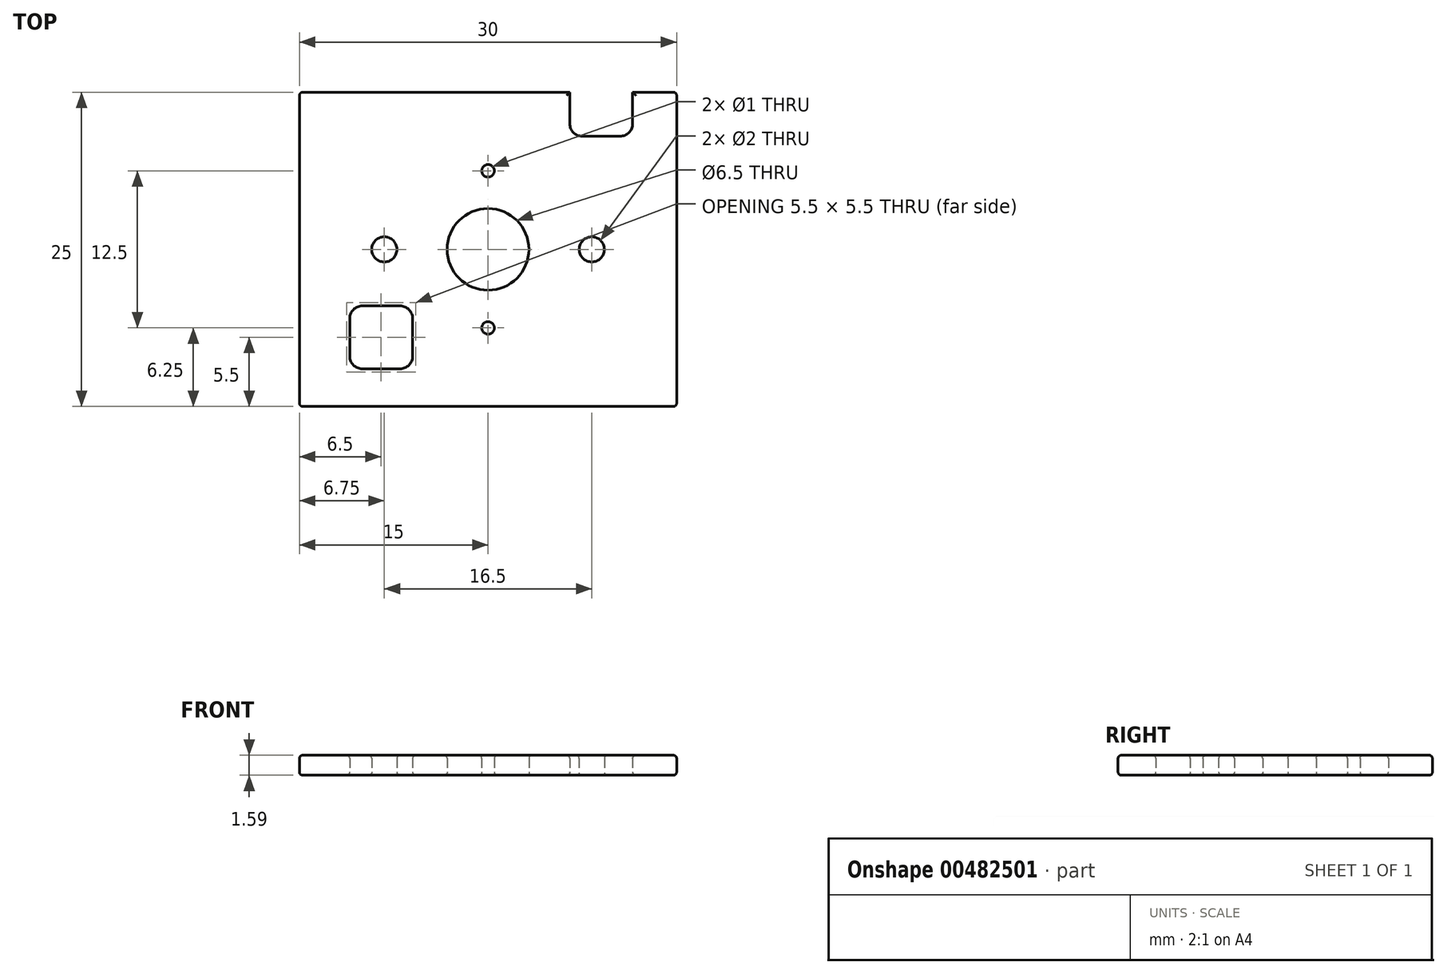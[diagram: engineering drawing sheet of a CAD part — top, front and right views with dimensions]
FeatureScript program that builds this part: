
annotation { "Feature Type Name" : "Feature", "Feature Type Description" : "" }
export const myFeature = defineFeature(function(context is Context, id is Id, definition is map)
    precondition{}
    {
        {
            var Q0;
            Q0=qCreatedBy(makeId("Top.planeOp"),FACE);
            var sketch = newSketch(context, id + "F0", { "sketchPlane" : qUnion([Q0])});
            skLineSegment(sketch, "E0", {"start": v(0, 0) * mm, "end": v(30, 0) * mm});
            skLineSegment(sketch, "E1", {"start": v(30, 0) * mm, "end": v(30, 25) * mm});
            skLineSegment(sketch, "E2", {"start": v(30, 25) * mm, "end": v(26.5, 25) * mm});
            skLineSegment(sketch, "E3", {"start": v(26.5, 25) * mm, "end": v(26.5, 21.5) * mm});
            skLineSegment(sketch, "E4", {"start": v(26.5, 21.5) * mm, "end": v(21.5, 21.5) * mm});
            skLineSegment(sketch, "E5", {"start": v(21.5, 21.5) * mm, "end": v(21.5, 25) * mm});
            skLineSegment(sketch, "E6", {"start": v(21.5, 25) * mm, "end": v(0, 25) * mm});
            skLineSegment(sketch, "E7", {"start": v(0, 25) * mm, "end": v(0, 0) * mm});
            skLineSegment(sketch, "E8.bottom", {"start": v(4, 8) * mm, "end": v(9, 8) * mm});
            skLineSegment(sketch, "E8.top", {"start": v(4, 3) * mm, "end": v(9, 3) * mm});
            skLineSegment(sketch, "E8.left", {"start": v(4, 8) * mm, "end": v(4, 3) * mm});
            skLineSegment(sketch, "E8.right", {"start": v(9, 8) * mm, "end": v(9, 3) * mm});
            skLineSegment(sketch, "E9", {"start": v(-15, 12.5) * mm, "end": v(45, 12.5) * mm, "construction": true});
            skLineSegment(sketch, "E10", {"start": v(15, 37.5) * mm, "end": v(15, -12.5) * mm, "construction": true});
            skCircle(sketch, "E11", {"center": v(15, 12.5) * mm, "radius": 3.25 * mm});
            skCircle(sketch, "E12", {"center": v(15, 6.25) * mm, "radius": 0.5 * mm});
            skCircle(sketch, "E13", {"center": v(6.75, 12.5) * mm, "radius": 1 * mm});
            skCircle(sketch, "E14.MirrorC", {"center": v(15, 18.75) * mm, "radius": 0.5 * mm});
            skCircle(sketch, "E15.MirrorC", {"center": v(23.25, 12.5) * mm, "radius": 1 * mm});
            skSolve(sketch);
        }
        {
            var Q0;
            Q0 = qSketchRegion(id + "F0", true);
            extrude(context, id + "F1", {"entities" : qUnion([Q0]), "depth" : 1.59 * mm});
        }
        {
            var Q0;
            Q0=makeQuery(id+"F1.opExtrude","SWEPT_EDGE",EDGE,{"disambiguationData":[OSD([sQuery(id+"F0.wireOp",EDGE,"E8.bottom"),sQuery(id+"F0.wireOp",EDGE,"E8.left")])]});
            var Q1;
            Q1=makeQuery(id+"F1.opExtrude","SWEPT_EDGE",EDGE,{"disambiguationData":[OSD([sQuery(id+"F0.wireOp",EDGE,"E8.bottom"),sQuery(id+"F0.wireOp",EDGE,"E8.right")])]});
            var Q2;
            Q2=makeQuery(id+"F1.opExtrude","SWEPT_EDGE",EDGE,{"disambiguationData":[OSD([sQuery(id+"F0.wireOp",EDGE,"E8.top"),sQuery(id+"F0.wireOp",EDGE,"E8.right")])]});
            var Q3;
            Q3=makeQuery(id+"F1.opExtrude","SWEPT_EDGE",EDGE,{"disambiguationData":[OSD([sQuery(id+"F0.wireOp",EDGE,"E8.top"),sQuery(id+"F0.wireOp",EDGE,"E8.left")])]});
            var Q4;
            Q4=makeQuery(id+"F1.opExtrude","SWEPT_EDGE",EDGE,{"disambiguationData":[OSD([sQuery(id+"F0.wireOp",EDGE,"E4"),sQuery(id+"F0.wireOp",EDGE,"E5")])]});
            var Q5;
            Q5=makeQuery(id+"F1.opExtrude","SWEPT_EDGE",EDGE,{"disambiguationData":[OSD([sQuery(id+"F0.wireOp",EDGE,"E3"),sQuery(id+"F0.wireOp",EDGE,"E4")])]});
            fillet(context, id + "F2", {"entities" : qUnion([Q0, Q1, Q2, Q3, Q4, Q5]), "radius" : 1 * mm, "tangentPropagation" : true, "allowEdgeOverflow" : false});
        }
        {
            var Q0;
            Q0=makeQuery(id+"F1.opExtrude","CAP_EDGE",EDGE,{"disambiguationData":[OSD([sQuery(id+"F0.wireOp",EDGE,"E13")])],"isStart":false});
            var Q1;
            Q1=makeQuery(id+"F1.opExtrude","CAP_EDGE",EDGE,{"disambiguationData":[OSD([sQuery(id+"F0.wireOp",EDGE,"E13")])],"isStart":true});
            var Q2;
            Q2=makeQuery(id+"F1.opExtrude","CAP_EDGE",EDGE,{"disambiguationData":[OSD([sQuery(id+"F0.wireOp",EDGE,"E14.MirrorC")])],"isStart":false});
            var Q3;
            Q3=makeQuery(id+"F1.opExtrude","CAP_EDGE",EDGE,{"disambiguationData":[OSD([sQuery(id+"F0.wireOp",EDGE,"E14.MirrorC")])],"isStart":true});
            var Q4;
            Q4=makeQuery(id+"F1.opExtrude","CAP_EDGE",EDGE,{"disambiguationData":[OSD([sQuery(id+"F0.wireOp",EDGE,"E15.MirrorC")])],"isStart":false});
            var Q5;
            Q5=makeQuery(id+"F1.opExtrude","CAP_EDGE",EDGE,{"disambiguationData":[OSD([sQuery(id+"F0.wireOp",EDGE,"E12")])],"isStart":false});
            var Q6;
            Q6=makeQuery(id+"F1.opExtrude","CAP_EDGE",EDGE,{"disambiguationData":[OSD([sQuery(id+"F0.wireOp",EDGE,"E12")])],"isStart":true});
            var Q7;
            Q7=makeQuery(id+"F1.opExtrude","CAP_EDGE",EDGE,{"disambiguationData":[OSD([sQuery(id+"F0.wireOp",EDGE,"E11")])],"isStart":false});
            var Q8;
            Q8=makeQuery(id+"F1.opExtrude","CAP_EDGE",EDGE,{"disambiguationData":[OSD([sQuery(id+"F0.wireOp",EDGE,"E11")])],"isStart":true});
            var Q9;
            Q9=makeQuery(id+"F1.opExtrude","CAP_EDGE",EDGE,{"disambiguationData":[OSD([sQuery(id+"F0.wireOp",EDGE,"E8.bottom")])],"isStart":false});
            var Q10;
            {var subQ0=sQuery(id+"F0.wireOp",EDGE,"E8.left");var subQ1=sQuery(id+"F0.wireOp",EDGE,"E8.bottom");Q10=makeQuery(id+"F2.opFillet","BLEND_EDGE",EDGE,{"blendedFrom":[makeQuery(id+"F1.opExtrude","SWEPT_EDGE",EDGE,{"disambiguationData":[OSD([subQ1,subQ0])]}),makeQuery(id+"F1.opExtrude","CAP_FACE",FACE,{"disambiguationData":[OSD([sQuery(id+"F0.wireOp",EDGE,"E0"),sQuery(id+"F0.wireOp",EDGE,"E1"),sQuery(id+"F0.wireOp",EDGE,"E2"),sQuery(id+"F0.wireOp",EDGE,"E3"),sQuery(id+"F0.wireOp",EDGE,"E4"),sQuery(id+"F0.wireOp",EDGE,"E5"),sQuery(id+"F0.wireOp",EDGE,"E6"),sQuery(id+"F0.wireOp",EDGE,"E7"),subQ1,sQuery(id+"F0.wireOp",EDGE,"E8.top"),subQ0,sQuery(id+"F0.wireOp",EDGE,"E8.right"),sQuery(id+"F0.wireOp",EDGE,"E11"),sQuery(id+"F0.wireOp",EDGE,"E12"),sQuery(id+"F0.wireOp",EDGE,"E13"),sQuery(id+"F0.wireOp",EDGE,"E14.MirrorC"),sQuery(id+"F0.wireOp",EDGE,"E15.MirrorC")])],"isStart":false})],"blendedInto":[makeQuery(id+"F1.opExtrude","CAP_FACE",FACE,{"disambiguationData":[OSD([sQuery(id+"F0.wireOp",EDGE,"E0"),sQuery(id+"F0.wireOp",EDGE,"E1"),sQuery(id+"F0.wireOp",EDGE,"E2"),sQuery(id+"F0.wireOp",EDGE,"E3"),sQuery(id+"F0.wireOp",EDGE,"E4"),sQuery(id+"F0.wireOp",EDGE,"E5"),sQuery(id+"F0.wireOp",EDGE,"E6"),sQuery(id+"F0.wireOp",EDGE,"E7"),subQ1,sQuery(id+"F0.wireOp",EDGE,"E8.top"),subQ0,sQuery(id+"F0.wireOp",EDGE,"E8.right"),sQuery(id+"F0.wireOp",EDGE,"E11"),sQuery(id+"F0.wireOp",EDGE,"E12"),sQuery(id+"F0.wireOp",EDGE,"E13"),sQuery(id+"F0.wireOp",EDGE,"E14.MirrorC"),sQuery(id+"F0.wireOp",EDGE,"E15.MirrorC")])],"isStart":false})]});}
            var Q11;
            Q11=makeQuery(id+"F1.opExtrude","CAP_EDGE",EDGE,{"disambiguationData":[OSD([sQuery(id+"F0.wireOp",EDGE,"E5")])],"isStart":false});
            var Q12;
            Q12=makeQuery(id+"F1.opExtrude","CAP_EDGE",EDGE,{"disambiguationData":[OSD([sQuery(id+"F0.wireOp",EDGE,"E2")])],"isStart":false});
            var Q13;
            Q13=makeQuery(id+"F1.opExtrude","CAP_EDGE",EDGE,{"disambiguationData":[OSD([sQuery(id+"F0.wireOp",EDGE,"E6")])],"isStart":false});
            var Q14;
            Q14=makeQuery(id+"F1.opExtrude","CAP_EDGE",EDGE,{"disambiguationData":[OSD([sQuery(id+"F0.wireOp",EDGE,"E7")])],"isStart":false});
            var Q15;
            Q15=makeQuery(id+"F1.opExtrude","SWEPT_EDGE",EDGE,{"disambiguationData":[OSD([sQuery(id+"F0.wireOp",EDGE,"E6"),sQuery(id+"F0.wireOp",EDGE,"E7")])]});
            var Q16;
            Q16=makeQuery(id+"F1.opExtrude","SWEPT_EDGE",EDGE,{"disambiguationData":[OSD([sQuery(id+"F0.wireOp",EDGE,"E1"),sQuery(id+"F0.wireOp",EDGE,"E2")])]});
            var Q17;
            Q17=makeQuery(id+"F1.opExtrude","SWEPT_EDGE",EDGE,{"disambiguationData":[OSD([sQuery(id+"F0.wireOp",EDGE,"E0"),sQuery(id+"F0.wireOp",EDGE,"E1")])]});
            var Q18;
            Q18=makeQuery(id+"F1.opExtrude","SWEPT_EDGE",EDGE,{"disambiguationData":[OSD([sQuery(id+"F0.wireOp",EDGE,"E0"),sQuery(id+"F0.wireOp",EDGE,"E7")])]});
            var Q19;
            Q19=makeQuery(id+"F1.opExtrude","CAP_EDGE",EDGE,{"disambiguationData":[OSD([sQuery(id+"F0.wireOp",EDGE,"E0")])],"isStart":false});
            var Q20;
            Q20=makeQuery(id+"F1.opExtrude","CAP_EDGE",EDGE,{"disambiguationData":[OSD([sQuery(id+"F0.wireOp",EDGE,"E1")])],"isStart":false});
            var Q21;
            Q21=makeQuery(id+"F1.opExtrude","CAP_EDGE",EDGE,{"disambiguationData":[OSD([sQuery(id+"F0.wireOp",EDGE,"E4")])],"isStart":true});
            var Q22;
            {var subQ0=sQuery(id+"F0.wireOp",EDGE,"E4");var subQ1=sQuery(id+"F0.wireOp",EDGE,"E3");Q22=makeQuery(id+"F2.opFillet","BLEND_EDGE",EDGE,{"blendedFrom":[makeQuery(id+"F1.opExtrude","SWEPT_EDGE",EDGE,{"disambiguationData":[OSD([subQ1,subQ0])]}),makeQuery(id+"F1.opExtrude","CAP_FACE",FACE,{"disambiguationData":[OSD([sQuery(id+"F0.wireOp",EDGE,"E0"),sQuery(id+"F0.wireOp",EDGE,"E1"),sQuery(id+"F0.wireOp",EDGE,"E2"),subQ1,subQ0,sQuery(id+"F0.wireOp",EDGE,"E5"),sQuery(id+"F0.wireOp",EDGE,"E6"),sQuery(id+"F0.wireOp",EDGE,"E7"),sQuery(id+"F0.wireOp",EDGE,"E8.bottom"),sQuery(id+"F0.wireOp",EDGE,"E8.top"),sQuery(id+"F0.wireOp",EDGE,"E8.left"),sQuery(id+"F0.wireOp",EDGE,"E8.right"),sQuery(id+"F0.wireOp",EDGE,"E11"),sQuery(id+"F0.wireOp",EDGE,"E12"),sQuery(id+"F0.wireOp",EDGE,"E13"),sQuery(id+"F0.wireOp",EDGE,"E14.MirrorC"),sQuery(id+"F0.wireOp",EDGE,"E15.MirrorC")])],"isStart":true})],"blendedInto":[makeQuery(id+"F1.opExtrude","CAP_FACE",FACE,{"disambiguationData":[OSD([sQuery(id+"F0.wireOp",EDGE,"E0"),sQuery(id+"F0.wireOp",EDGE,"E1"),sQuery(id+"F0.wireOp",EDGE,"E2"),subQ1,subQ0,sQuery(id+"F0.wireOp",EDGE,"E5"),sQuery(id+"F0.wireOp",EDGE,"E6"),sQuery(id+"F0.wireOp",EDGE,"E7"),sQuery(id+"F0.wireOp",EDGE,"E8.bottom"),sQuery(id+"F0.wireOp",EDGE,"E8.top"),sQuery(id+"F0.wireOp",EDGE,"E8.left"),sQuery(id+"F0.wireOp",EDGE,"E8.right"),sQuery(id+"F0.wireOp",EDGE,"E11"),sQuery(id+"F0.wireOp",EDGE,"E12"),sQuery(id+"F0.wireOp",EDGE,"E13"),sQuery(id+"F0.wireOp",EDGE,"E14.MirrorC"),sQuery(id+"F0.wireOp",EDGE,"E15.MirrorC")])],"isStart":true})]});}
            var Q23;
            Q23=makeQuery(id+"F1.opExtrude","CAP_EDGE",EDGE,{"disambiguationData":[OSD([sQuery(id+"F0.wireOp",EDGE,"E2")])],"isStart":true});
            var Q24;
            Q24=makeQuery(id+"F1.opExtrude","CAP_EDGE",EDGE,{"disambiguationData":[OSD([sQuery(id+"F0.wireOp",EDGE,"E1")])],"isStart":true});
            var Q25;
            Q25=makeQuery(id+"F1.opExtrude","CAP_EDGE",EDGE,{"disambiguationData":[OSD([sQuery(id+"F0.wireOp",EDGE,"E0")])],"isStart":true});
            var Q26;
            Q26=makeQuery(id+"F1.opExtrude","CAP_EDGE",EDGE,{"disambiguationData":[OSD([sQuery(id+"F0.wireOp",EDGE,"E7")])],"isStart":true});
            var Q27;
            Q27=makeQuery(id+"F1.opExtrude","CAP_EDGE",EDGE,{"disambiguationData":[OSD([sQuery(id+"F0.wireOp",EDGE,"E6")])],"isStart":true});
            var Q28;
            Q28=makeQuery(id+"F1.opExtrude","CAP_EDGE",EDGE,{"disambiguationData":[OSD([sQuery(id+"F0.wireOp",EDGE,"E8.top")])],"isStart":true});
            fillet(context, id + "F3", {"entities" : qUnion([Q0, Q1, Q2, Q3, Q4, Q5, Q6, Q7, Q8, Q9, Q10, Q11, Q12, Q13, Q14, Q15, Q16, Q17, Q18, Q19, Q20, Q21, Q22, Q23, Q24, Q25, Q26, Q27, Q28]), "radius" : .25 * mm, "tangentPropagation" : true, "allowEdgeOverflow" : false});
        }
    });
